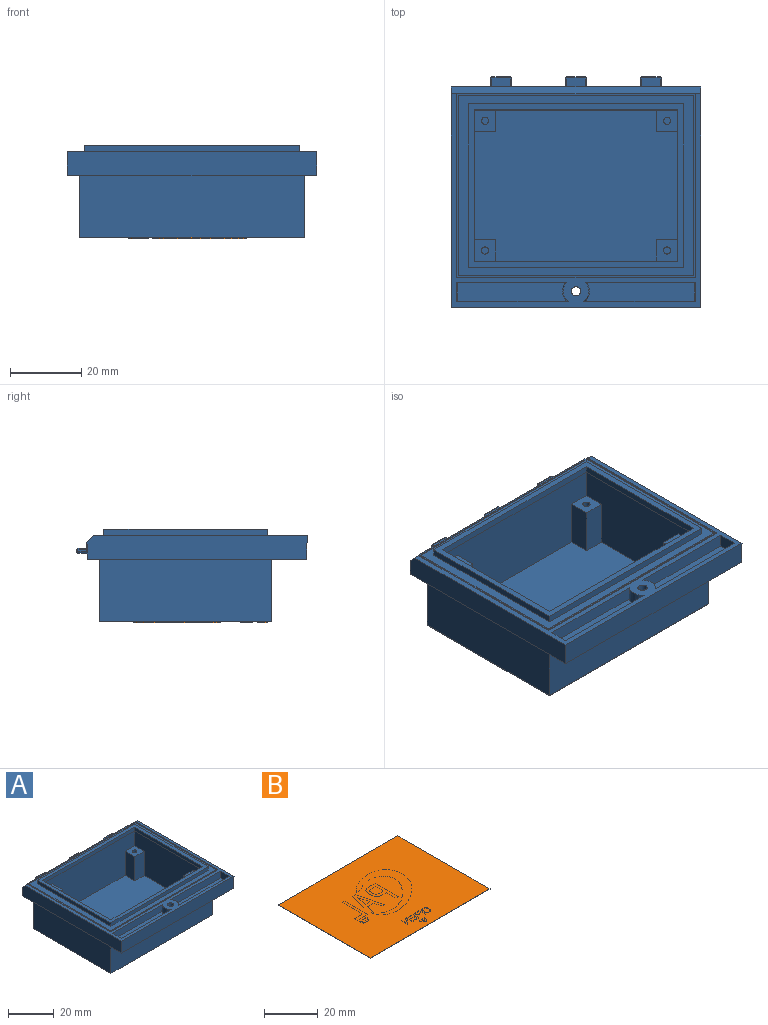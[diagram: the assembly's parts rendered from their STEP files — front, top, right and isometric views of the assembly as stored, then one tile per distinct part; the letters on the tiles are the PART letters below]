
ASSEMBLY  parts=2 mates=1
PART A: 126 faces, bbox 70x64.6x25.9 mm
  f0: plane 69.77x61.57mm, normal (0,0,-1), area 1213.8mm2, adj f1,f32,f48,f61,f83,f101,f102,f103
  f1: plane 69.94x4.55mm, normal (0,1,-0.02), area 187.9mm2, adj f0,f2,f8,f11,f20,f25,f27,f29
  f2: cylinder r=0.3mm len=2.58mm, axis (0,-1,0), area 1.2mm2, adj f1,f69,f77,f93
  f3: sphere r=0.3mm, area 0.1mm2, adj f30,f68,f82
  f4: sphere r=0.3mm, area 0.1mm2, adj f22,f23,f62
  f5: plane 5.2x2.47mm, normal (0,0,1), area 12.8mm2, adj f9,f24,f31,f81
  f6: cylinder r=0.3mm len=0.7mm, axis (0,0,1), area 0.3mm2, adj f20,f36,f66,f80
  f7: cylinder r=1.3mm len=5.2mm, axis (0,0,1), area 42.5mm2, adj f32,f85
  f8: cylinder r=0.3mm len=2.58mm, axis (0,-1,0), area 1.2mm2, adj f1,f29,f76,f93
  f9: plane 54x2.15mm, normal (0,1,0.01), area 104.9mm2, adj f5,f10,f11,f20,f23,f24,f25,f27
  f10: cylinder r=0.3mm len=2.47mm, axis (0,-1,0), area 1.2mm2, adj f9,f35,f70,f75
  f11: plane 15.2x0.11mm, normal (0,0,-1), area 1.7mm2, adj f1,f9,f20,f77
  f12: plane 66x0.2mm, normal (0,-1,0), area 13.2mm2, adj f37,f41,f44,f57
  f13: plane 42.4x1.9mm, normal (-1,0,0.02), area 80.5mm2, adj f16,f21,f52,f98
  f14: plane 45.8x1.9mm, normal (-1,0,0), area 87mm2, adj f17,f44,f52,f53
  f15: cylinder r=0.3mm len=0.7mm, axis (0,0,1), area 0.3mm2, adj f35,f72,f74,f75
  f16: plane 57.1x1.9mm, normal (0,-1,0.02), area 108.4mm2, adj f13,f52,f86,f97
  f17: plane 60.5x1.9mm, normal (0,-1,0), area 114.9mm2, adj f14,f44,f52,f54
  f18: sphere r=0.3mm, area 0.1mm2, adj f31,f81,f82
  f19: cylinder r=0.3mm len=0.7mm, axis (0,0,-1), area 0.3mm2, adj f60,f69,f73,f77
  f20: plane 2.58x0.7mm, normal (1,0,0), area 1.8mm2, adj f1,f6,f9,f11,f24,f79
  f21: plane 57.1x1.9mm, normal (0,1,0.02), area 108.4mm2, adj f13,f52,f86,f100
  f22: cylinder r=0.3mm len=0.7mm, axis (0,0,-1), area 0.3mm2, adj f4,f29,f73,f76
  f23: cylinder r=0.3mm len=2.47mm, axis (0,1,0), area 1.2mm2, adj f4,f9,f29,f71
  f24: cylinder r=0.3mm len=2.47mm, axis (0,-1,0), area 1.2mm2, adj f5,f9,f20,f80
  f25: plane 2.58x0.7mm, normal (-1,0,0), area 1.8mm2, adj f1,f9,f30,f31,f82,f89
  f26: plane 66.8x0.2mm, normal (0,-1,0), area 13.4mm2, adj f28,f34,f37,f85
  f27: plane 2.2x0.11mm, normal (-1,0,0), area 0.2mm2, adj f1,f9,f84,f87
  f28: plane 51.5x0.3mm, normal (-1,0,0), area 10.3mm2, adj f26,f37,f59,f84,f85
  f29: plane 2.58x0.7mm, normal (1,0,0), area 1.8mm2, adj f1,f8,f9,f22,f23,f88
  f30: cylinder r=0.3mm len=2.58mm, axis (0,-1,0), area 1.2mm2, adj f1,f3,f25,f94
  f31: cylinder r=0.3mm len=2.47mm, axis (0,1,0), area 1.2mm2, adj f5,f9,f18,f25
  f32: cone r=2.15mm half-angle=52.6deg, axis (0,0,-1), area 28.9mm2, adj f0,f7
  f33: plane 5.5x3.6mm, normal (-1,0,0.03), area 19.4mm2, adj f42,f45,f50,f85
  f34: plane 51.5x0.3mm, normal (1,0,0), area 10.3mm2, adj f26,f37,f59,f84,f85
  f35: plane 2.58x0.7mm, normal (1,0,0), area 1.8mm2, adj f1,f9,f10,f15,f89,f95
  f36: sphere r=0.3mm, area 0.1mm2, adj f6,f68,f79
  f37: plane 66.8x51.5mm, normal (0,0,1), area 94mm2, adj f12,f26,f28,f34,f41,f56,f57,f59
  f38: sphere r=0.3mm, area 0.1mm2, adj f39,f40,f64
  f39: cylinder r=0.3mm len=5.2mm, axis (1,0,0), area 2.5mm2, adj f38,f70,f72,f75
  f40: cylinder r=0.3mm len=2.47mm, axis (0,-1,0), area 1.2mm2, adj f9,f38,f70,f90
  f41: plane 50.7x0.2mm, normal (1,0,0), area 10.1mm2, adj f12,f37,f44,f56
  f42: plane 30.92x3.63mm, normal (0,-1,0.03), area 110.5mm2, adj f33,f50,f58,f85
  f43: plane 30.92x3.63mm, normal (0,-1,0.03), area 110.5mm2, adj f46,f49,f51,f85
  f44: plane 66x50.7mm, normal (0,0,1), area 575.3mm2, adj f12,f14,f17,f41,f53,f54,f56,f57
  f45: plane 31.39x3.64mm, normal (0,1,0.03), area 112mm2, adj f33,f50,f58,f85
  f46: plane 5.5x3.6mm, normal (1,0,0.03), area 19.4mm2, adj f43,f47,f49,f85
  f47: plane 31.39x3.64mm, normal (0,1,0.03), area 112mm2, adj f46,f49,f51,f85
  f48: plane 61.77x6.5mm, normal (1,0,-0.02), area 399.1mm2, adj f0,f1,f83,f84,f85
  f49: plane 30.87x5.25mm, normal (0,0,1), area 157.1mm2, adj f43,f46,f47,f51
  f50: plane 30.87x5.25mm, normal (0,0,1), area 157.1mm2, adj f33,f42,f45,f58
  f51: cone r=3.71mm half-angle=2deg, axis (0,0,-1), area 21.8mm2, adj f43,f47,f49,f85
  f52: plane 60.5x45.8mm, normal (0,0,1), area 349.9mm2, adj f13,f14,f16,f17,f21,f53,f54,f86
  f53: plane 60.5x1.9mm, normal (0,1,0), area 114.9mm2, adj f14,f44,f52,f54
  f54: plane 45.8x1.9mm, normal (1,0,0), area 87mm2, adj f17,f44,f52,f53
  f55: plane 2.2x0.11mm, normal (1,0,0), area 0.2mm2, adj f1,f9,f84,f88
  f56: plane 66x0.2mm, normal (0,1,0), area 13.2mm2, adj f37,f41,f44,f57
  f57: plane 50.7x0.2mm, normal (-1,0,0), area 10.1mm2, adj f12,f37,f44,f56
  f58: cone r=3.71mm half-angle=2deg, axis (0,0,-1), area 21.8mm2, adj f42,f45,f50,f85
  f59: plane 66.8x0.3mm, normal (0,1,0), area 20mm2, adj f28,f34,f37,f84
  f60: sphere r=0.3mm, area 0.1mm2, adj f19,f62,f78
  f61: plane 61.77x6.5mm, normal (-1,0,-0.02), area 399.1mm2, adj f0,f1,f83,f84,f85
  f62: cylinder r=0.3mm len=5.2mm, axis (1,0,0), area 2.5mm2, adj f4,f60,f71,f73
  f63: sphere r=0.3mm, area 0.1mm2, adj f64,f65,f91
  f64: cylinder r=0.3mm len=0.7mm, axis (0,0,1), area 0.3mm2, adj f38,f63,f72,f90
  f65: cylinder r=0.3mm len=5.2mm, axis (1,0,0), area 2.5mm2, adj f63,f72,f74,f92
  f66: plane 5.2x0.7mm, normal (0,1,0), area 3.6mm2, adj f6,f68,f81,f82
  f67: cylinder r=0.3mm len=5.2mm, axis (1,0,0), area 2.5mm2, adj f69,f73,f76,f93
  f68: cylinder r=0.3mm len=5.2mm, axis (1,0,0), area 2.5mm2, adj f3,f36,f66,f94
  f69: sphere r=0.3mm, area 0.1mm2, adj f2,f19,f67
  f70: plane 5.2x2.47mm, normal (0,0,1), area 12.8mm2, adj f9,f10,f39,f40
  f71: plane 5.2x2.47mm, normal (0,0,1), area 12.8mm2, adj f9,f23,f62,f78
  f72: plane 5.2x0.7mm, normal (0,1,0), area 3.6mm2, adj f15,f39,f64,f65
  f73: plane 5.2x0.7mm, normal (0,1,0), area 3.6mm2, adj f19,f22,f62,f67
  f74: sphere r=0.3mm, area 0.1mm2, adj f15,f65,f95
  f75: sphere r=0.3mm, area 0.1mm2, adj f10,f15,f39
  f76: sphere r=0.3mm, area 0.1mm2, adj f8,f22,f67
  f77: plane 2.58x0.7mm, normal (-1,0,0), area 1.8mm2, adj f1,f2,f9,f11,f19,f78
  f78: cylinder r=0.3mm len=2.47mm, axis (0,1,0), area 1.2mm2, adj f9,f60,f71,f77
  f79: cylinder r=0.3mm len=2.58mm, axis (0,1,0), area 1.2mm2, adj f1,f20,f36,f94
  f80: sphere r=0.3mm, area 0.1mm2, adj f6,f24,f81
  f81: cylinder r=0.3mm len=5.2mm, axis (1,0,0), area 2.5mm2, adj f5,f18,f66,f80
  f82: cylinder r=0.3mm len=0.7mm, axis (0,0,-1), area 0.3mm2, adj f3,f18,f25,f66
  f83: plane 70x6.5mm, normal (0,-1,-0.02), area 454.3mm2, adj f0,f48,f61,f85
  f84: plane 70x2.02mm, normal (0,0.7,0.71), area 188.2mm2, adj f1,f9,f27,f28,f34,f48,f55,f59
  f85: plane 70x59.8mm, normal (0,0,1), area 414.5mm2, adj f7,f26,f28,f33,f34,f42,f43,f45
  f86: plane 42.4x1.9mm, normal (1,0,0.02), area 80.5mm2, adj f16,f21,f52,f99
  f87: plane 3.1x0.11mm, normal (0,0,-1), area 0.3mm2, adj f1,f9,f27,f90
  f88: plane 3.1x0.11mm, normal (0,0,-1), area 0.3mm2, adj f1,f9,f29,f55
  f89: plane 15.2x0.11mm, normal (0,0,-1), area 1.7mm2, adj f1,f9,f25,f35
  f90: plane 2.58x0.7mm, normal (-1,0,0), area 1.8mm2, adj f1,f9,f40,f64,f87,f91
  f91: cylinder r=0.3mm len=2.58mm, axis (0,1,0), area 1.2mm2, adj f1,f63,f90,f92
  f92: plane 5.2x2.58mm, normal (0,0,-1), area 13.4mm2, adj f1,f65,f91,f95
  f93: plane 5.2x2.58mm, normal (0,0,-1), area 13.4mm2, adj f1,f2,f8,f67
  f94: plane 5.2x2.58mm, normal (0,0,-1), area 13.4mm2, adj f1,f30,f68,f79
  f95: cylinder r=0.3mm len=2.58mm, axis (0,1,0), area 1.2mm2, adj f1,f35,f74,f92
  f96: plane 57.03x42.33mm, normal (0,0,1), area 2272.4mm2, adj f97,f98,f99,f100,f106,f108,f111,f112
  f97: plane 57.03x21mm, normal (0,-1,0), area 1012.6mm2, adj f16,f96,f98,f99,f108,f109,f117,f119
  f98: plane 42.33x21mm, normal (-1,0,0), area 704.2mm2, adj f13,f96,f97,f100,f106,f109,f121,f124
  f99: plane 42.33x21mm, normal (1,0,0), area 703.9mm2, adj f86,f96,f97,f100,f111,f114,f116,f119
  f100: plane 57.03x21mm, normal (0,1,0), area 1013.8mm2, adj f21,f96,f98,f99,f112,f114,f122,f124
  f101: plane 63.1x17.5mm, normal (0,-1,0), area 1104.3mm2, adj f0,f102,f104,f105
  f102: plane 48.4x17.5mm, normal (-1,0,0), area 847mm2, adj f0,f101,f103,f105
  f103: plane 63.1x17.5mm, normal (0,1,0), area 1104.3mm2, adj f0,f102,f104,f105
  f104: plane 48.4x17.5mm, normal (1,0,0), area 847mm2, adj f0,f101,f103,f105
  f105: plane 63.1x48.4mm, normal (0,0,-1), area 3054mm2, adj f101,f102,f103,f104
  f106: plane 13x5.93mm, normal (0,-1,0), area 77.1mm2, adj f96,f98,f108,f109
  f107: cylinder r=1mm len=13mm, axis (0,0,-1), area 81.7mm2, adj f109,f110
  f108: plane 13x6mm, normal (-1,0,0), area 78mm2, adj f96,f97,f106,f109
  f109: plane 6x5.93mm, normal (0,0,1), area 32.5mm2, adj f97,f98,f106,f107,f108
  f110: plane 2x2mm, normal (0,0,1), area 3.1mm2, adj f107
  f111: plane 13x5.93mm, normal (0,1,0), area 77.1mm2, adj f96,f99,f112,f114
  f112: plane 13x5.93mm, normal (1,0,0), area 77.1mm2, adj f96,f100,f111,f114
  f113: cylinder r=1mm len=13mm, axis (0,0,-1), area 81.7mm2, adj f114,f115
  f114: plane 5.93x5.93mm, normal (0,0,1), area 32.1mm2, adj f99,f100,f111,f112,f113
  f115: plane 2x2mm, normal (0,0,1), area 3.1mm2, adj f113
  f116: plane 18x6mm, normal (0,-1,0), area 108mm2, adj f96,f99,f117,f119
  f117: plane 18x6mm, normal (1,0,0), area 108mm2, adj f96,f97,f116,f119
  f118: cylinder r=1mm len=18mm, axis (0,0,-1), area 113.1mm2, adj f119,f120
  f119: plane 6x6mm, normal (0,0,1), area 32.9mm2, adj f97,f99,f116,f117,f118
  f120: plane 2x2mm, normal (0,0,1), area 3.1mm2, adj f118
  f121: plane 18x5.93mm, normal (0,1,0), area 106.8mm2, adj f96,f98,f122,f124
  f122: plane 18x5.93mm, normal (-1,0,0), area 106.8mm2, adj f96,f100,f121,f124
  f123: cylinder r=1mm len=18mm, axis (0,0,-1), area 113.1mm2, adj f124,f125
  f124: plane 5.93x5.93mm, normal (0,0,1), area 32.1mm2, adj f98,f100,f121,f122,f123
  f125: plane 2x2mm, normal (0,0,1), area 3.1mm2, adj f123
PART B: 192 faces, bbox 63.1x48.4x0.4 mm
  f0: plane 2.86x0.41mm, normal (0,0,-1), area 1.1mm2, adj f8,f9,f10,f11
  f1: plane 0.56x0.41mm, normal (0,0,-1), area 0.1mm2, adj f12,f13,f14
  f2: plane 1.33x0.41mm, normal (0,0,-1), area 0.4mm2, adj f15,f16,f17,f18
  f3: plane 2.09x0.41mm, normal (0,0,-1), area 0.7mm2, adj f19,f20,f21,f22
  f4: plane 4.04x3.98mm, normal (0,0,-1), area 14.9mm2, adj f23,f24,f25,f26,f27,f28,f29
  f5: plane 5.29x2.59mm, normal (0,0,-1), area 6.9mm2, adj f30,f31,f32
  f6: plane 1.82x1.12mm, normal (0,0,-1), area 1.9mm2, adj f33,f34,f35,f36,f37,f38,f39,f40
  f7: plane 2.61x2.04mm, normal (0,0,-1), area 4.8mm2, adj f43,f44,f45,f46,f47,f48,f49,f50
  f8: plane 0.41x0.28mm, normal (-0.83,0.56,0), area 0.1mm2, adj f0,f9,f11,f63
  f9: plane 2.3x0.2mm, normal (0,1,0), area 0.5mm2, adj f0,f8,f10,f63
  f10: plane 0.41x0.28mm, normal (0.83,0.56,0), area 0.1mm2, adj f0,f9,f11,f63
  f11: plane 2.86x0.2mm, normal (0,-1,0), area 0.6mm2, adj f0,f8,f10,f63
  f12: plane 0.41x0.28mm, normal (0.83,0.56,0), area 0.1mm2, adj f1,f13,f14,f63
  f13: plane 0.56x0.2mm, normal (0,-1,0), area 0.1mm2, adj f1,f12,f14,f63
  f14: plane 0.41x0.28mm, normal (-0.83,0.56,0), area 0.1mm2, adj f1,f12,f13,f63
  f15: plane 0.41x0.28mm, normal (0.83,0.56,0), area 0.1mm2, adj f2,f16,f18,f63
  f16: plane 1.33x0.2mm, normal (0,-1,0), area 0.3mm2, adj f2,f15,f17,f63
  f17: plane 0.41x0.28mm, normal (-0.83,0.56,0), area 0.1mm2, adj f2,f16,f18,f63
  f18: plane 0.77x0.2mm, normal (0,1,0), area 0.2mm2, adj f2,f15,f17,f63
  f19: plane 0.41x0.28mm, normal (0.83,0.56,0), area 0.1mm2, adj f3,f20,f22,f63
  f20: plane 2.09x0.2mm, normal (0,-1,0), area 0.4mm2, adj f3,f19,f21,f63
  f21: plane 0.41x0.28mm, normal (-0.83,0.56,0), area 0.1mm2, adj f3,f20,f22,f63
  f22: plane 1.53x0.2mm, normal (0,1,0), area 0.3mm2, adj f3,f19,f21,f63
  f23: cylinder r=3.28mm len=0.99mm, axis (0,0,-1), area 0.3mm2, adj f4,f24,f29,f65
  f24: extruded ~1.99x1.68mm, area 0.9mm2, adj f4,f23,f25,f65
  f25: plane 2.3x0.3mm, normal (0,-1,0), area 0.7mm2, adj f4,f24,f26,f65
  f26: plane 4.04x0.3mm, normal (-1,0,0), area 1.2mm2, adj f4,f25,f27,f65
  f27: plane 1.82x0.3mm, normal (0,1,0), area 0.5mm2, adj f4,f26,f28,f65
  f28: extruded ~1.51x0.3mm, area 0.5mm2, adj f4,f27,f29,f65
  f29: cylinder r=1.62mm len=0.76mm, axis (0,0,-1), area 0.3mm2, adj f4,f23,f28,f65
  f30: plane 5.29x1.3mm, normal (-0.97,-0.24,0), area 1.6mm2, adj f5,f31,f32,f66
  f31: plane 2.59x0.3mm, normal (0,1,0), area 0.8mm2, adj f5,f30,f32,f66
  f32: plane 5.29x1.29mm, normal (0.97,-0.24,0), area 1.6mm2, adj f5,f30,f31,f66
  f33: plane 1.39x0.3mm, normal (0,1,0), area 0.4mm2, adj f6,f34,f42,f72
  f34: plane 0.3x0.22mm, normal (0.32,0.95,0), area 0.1mm2, adj f6,f33,f35,f72
  f35: plane 0.3x0.15mm, normal (0.71,0.7,0), area 0.1mm2, adj f6,f34,f36,f72
  f36: plane 0.3x0.22mm, normal (0.95,0.31,0), area 0.1mm2, adj f6,f35,f37,f72
  f37: plane 0.3x0.22mm, normal (1,0,0), area 0.1mm2, adj f6,f36,f38,f72
  f38: plane 0.3x0.22mm, normal (0.95,-0.31,0), area 0.1mm2, adj f6,f37,f39,f72
  f39: plane 0.3x0.15mm, normal (0.71,-0.7,0), area 0.1mm2, adj f6,f38,f40,f72
  f40: plane 0.3x0.22mm, normal (0.32,-0.95,0), area 0.1mm2, adj f6,f39,f41,f72
  f41: plane 1.39x0.3mm, normal (0,-1,0), area 0.4mm2, adj f6,f40,f42,f72
  f42: plane 1.12x0.3mm, normal (-1,0,0), area 0.3mm2, adj f6,f33,f41,f72
  f43: plane 0.58x0.3mm, normal (0,1,0), area 0.2mm2, adj f7,f44,f62,f73
  f44: plane 0.3x0.29mm, normal (0.25,0.97,0), area 0.1mm2, adj f7,f43,f45,f73
  f45: plane 0.3x0.22mm, normal (0.56,0.83,0), area 0.1mm2, adj f7,f44,f46,f73
  f46: plane 0.3x0.22mm, normal (0.84,0.55,0), area 0.1mm2, adj f7,f45,f47,f73
  f47: plane 0.3x0.3mm, normal (0.97,0.24,0), area 0.1mm2, adj f7,f46,f48,f73
  f48: plane 1.12x0.3mm, normal (1,0,0), area 0.3mm2, adj f7,f47,f49,f73
  f49: plane 0.3x0.3mm, normal (0.97,-0.24,0), area 0.1mm2, adj f7,f48,f50,f73
  f50: plane 0.3x0.22mm, normal (0.84,-0.55,0), area 0.1mm2, adj f7,f49,f51,f73
  f51: plane 0.3x0.22mm, normal (0.56,-0.83,0), area 0.1mm2, adj f7,f50,f52,f73
  f52: plane 0.3x0.29mm, normal (0.25,-0.97,0), area 0.1mm2, adj f7,f51,f53,f73
  f53: plane 0.58x0.3mm, normal (0,-1,0), area 0.2mm2, adj f7,f52,f54,f73
  f54: plane 0.3x0.29mm, normal (-0.25,-0.97,0), area 0.1mm2, adj f7,f53,f55,f73
  f55: plane 0.3x0.22mm, normal (-0.56,-0.83,0), area 0.1mm2, adj f7,f54,f56,f73
  f56: plane 0.3x0.22mm, normal (-0.84,-0.55,0), area 0.1mm2, adj f7,f55,f57,f73
  f57: plane 0.3x0.3mm, normal (-0.97,-0.24,0), area 0.1mm2, adj f7,f56,f58,f73
  f58: plane 1.12x0.3mm, normal (-1,0,0), area 0.3mm2, adj f7,f57,f59,f73
  f59: plane 0.3x0.3mm, normal (-0.97,0.24,0), area 0.1mm2, adj f7,f58,f60,f73
  f60: plane 0.3x0.22mm, normal (-0.84,0.55,0), area 0.1mm2, adj f7,f59,f61,f73
  f61: plane 0.3x0.22mm, normal (-0.56,0.83,0), area 0.1mm2, adj f7,f60,f62,f73
  f62: plane 0.3x0.29mm, normal (-0.25,0.97,0), area 0.1mm2, adj f7,f43,f61,f73
  f63: plane 3.8x2.8mm, normal (0,0,-1), area 3mm2, adj f8,f9,f10,f11,f12,f13,f14,f15
  f64: plane 26.09x24.59mm, normal (0,0,-1), area 159.6mm2, adj f77,f78,f79,f80
  f65: plane 12.21x6.45mm, normal (0,0,-1), area 33.8mm2, adj f23,f24,f25,f26,f27,f28,f29,f81
  f66: plane 12.2x7.77mm, normal (0,0,-1), area 34.6mm2, adj f30,f31,f32,f91,f92,f93,f94,f95
  f67: plane 12.2x5.55mm, normal (0,0,-1), area 21.7mm2, adj f99,f100,f101,f102,f103,f104
  f68: plane 2x1.58mm, normal (0,0,-1), area 0.8mm2, adj f105,f106,f107,f108,f109,f110,f111,f112
  f69: plane 2x2mm, normal (0,0,-1), area 2mm2, adj f113,f114,f115,f116,f117,f118,f119,f120
  f70: plane 3.5x2.92mm, normal (0,0,-1), area 4.7mm2, adj f126,f127,f128,f129,f130,f131,f132,f133
  f71: plane 3.5x2.63mm, normal (0,0,-1), area 4.3mm2, adj f136,f137,f138,f139,f140,f141,f142,f143
  f72: plane 3.5x2.7mm, normal (0,0,-1), area 3.5mm2, adj f33,f34,f35,f36,f37,f38,f39,f40
  f73: plane 3.5x2.92mm, normal (0,0,-1), area 4.1mm2, adj f43,f44,f45,f46,f47,f48,f49,f50
  f74: plane 2.8x1.9mm, normal (-0.83,-0.56,0), area 1mm2, adj f63,f75,f76,f186
  f75: plane 3.8x0.3mm, normal (0,1,0), area 1.1mm2, adj f63,f74,f76,f186
  f76: plane 2.8x1.9mm, normal (0.83,-0.56,0), area 1mm2, adj f63,f74,f75,f186
  f77: plane 2.16x0.3mm, normal (0,-1,0), area 0.6mm2, adj f64,f78,f80,f186
  f78: extruded ~25.91x24.22mm, area 19.1mm2, adj f64,f77,f79,f186
  f79: plane 0.48x0.3mm, normal (0,1,0), area 0.1mm2, adj f64,f78,f80,f186
  f80: extruded ~21.1x19.29mm, area 14.1mm2, adj f64,f77,f79,f186
  f81: extruded ~1.24x0.89mm, area 0.5mm2, adj f65,f82,f90,f186
  f82: extruded ~1.99x0.48mm, area 0.6mm2, adj f65,f81,f83,f186
  f83: plane 3.26x0.3mm, normal (0,1,0), area 1mm2, adj f65,f82,f84,f186
  f84: plane 12.2x0.3mm, normal (1,0,0), area 3.7mm2, adj f65,f83,f85,f186
  f85: plane 1.23x0.3mm, normal (0,-1,0), area 0.4mm2, adj f65,f84,f86,f186
  f86: plane 5.04x0.3mm, normal (-1,0,0), area 1.5mm2, adj f65,f85,f87,f186
  f87: plane 2.46x0.3mm, normal (0,-1,0), area 0.7mm2, adj f65,f86,f88,f186
  f88: extruded ~2.05x0.98mm, area 0.7mm2, adj f65,f87,f89,f186
  f89: extruded ~2.66x0.7mm, area 0.8mm2, adj f65,f88,f90,f186
  f90: extruded ~1.8x0.3mm, area 0.5mm2, adj f65,f81,f89,f186
  f91: plane 1.37x0.3mm, normal (0,-1,0), area 0.4mm2, adj f66,f92,f98,f186
  f92: plane 3.53x0.85mm, normal (-0.97,-0.23,0), area 1.1mm2, adj f66,f91,f93,f186
  f93: plane 3.32x0.3mm, normal (0,-1,0), area 1mm2, adj f66,f92,f94,f186
  f94: plane 3.53x0.85mm, normal (0.97,-0.23,0), area 1.1mm2, adj f66,f93,f95,f186
  f95: plane 1.37x0.3mm, normal (0,-1,0), area 0.4mm2, adj f66,f94,f96,f186
  f96: plane 12.2x3.16mm, normal (-0.97,0.25,0), area 3.8mm2, adj f66,f95,f97,f186
  f97: plane 1.44x0.3mm, normal (0,1,0), area 0.4mm2, adj f66,f96,f98,f186
  f98: plane 12.2x3.16mm, normal (0.97,0.25,0), area 3.8mm2, adj f66,f91,f97,f186
  f99: plane 5.55x0.3mm, normal (0,-1,0), area 1.7mm2, adj f67,f100,f104,f186
  f100: plane 1.56x0.3mm, normal (-1,0,0), area 0.5mm2, adj f67,f99,f101,f186
  f101: plane 4.32x0.3mm, normal (0,1,0), area 1.3mm2, adj f67,f100,f102,f186
  f102: plane 10.64x0.3mm, normal (-1,0,0), area 3.2mm2, adj f67,f101,f103,f186
  f103: plane 1.23x0.3mm, normal (0,1,0), area 0.4mm2, adj f67,f102,f104,f186
  f104: plane 12.2x0.3mm, normal (1,0,0), area 3.7mm2, adj f67,f99,f103,f186
  f105: plane 0.67x0.3mm, normal (0,-1,0), area 0.2mm2, adj f68,f106,f112,f186
  f106: plane 0.3x0.21mm, normal (-1,0,0), area 0.1mm2, adj f68,f105,f107,f186
  f107: plane 1.58x0.3mm, normal (0,1,0), area 0.5mm2, adj f68,f106,f108,f186
  f108: plane 0.3x0.21mm, normal (1,0,0), area 0.1mm2, adj f68,f107,f109,f186
  f109: plane 0.67x0.3mm, normal (0,-1,0), area 0.2mm2, adj f68,f108,f110,f186
  f110: plane 1.79x0.3mm, normal (1,0,0), area 0.5mm2, adj f68,f109,f111,f186
  f111: plane 0.3x0.25mm, normal (0,-1,0), area 0.1mm2, adj f68,f110,f112,f186
  f112: plane 1.79x0.3mm, normal (-1,0,0), area 0.5mm2, adj f68,f105,f111,f186
  f113: plane 1.57x0.3mm, normal (-1,0,0), area 0.5mm2, adj f69,f114,f125,f186
  f114: plane 1.57x0.58mm, normal (0.94,-0.35,0), area 0.5mm2, adj f69,f113,f115,f186
  f115: plane 0.33x0.3mm, normal (0,-1,0), area 0.1mm2, adj f69,f114,f116,f186
  f116: plane 1.57x0.58mm, normal (-0.94,-0.35,0), area 0.5mm2, adj f69,f115,f117,f186
  f117: plane 1.57x0.3mm, normal (1,0,0), area 0.5mm2, adj f69,f116,f118,f186
  f118: plane 0.3x0.25mm, normal (0,-1,0), area 0.1mm2, adj f69,f117,f119,f186
  f119: plane 2x0.3mm, normal (-1,0,0), area 0.6mm2, adj f69,f118,f120,f186
  f120: plane 0.38x0.3mm, normal (0,1,0), area 0.1mm2, adj f69,f119,f121,f186
  f121: plane 1.79x0.63mm, normal (0.94,0.33,0), area 0.6mm2, adj f69,f120,f122,f186
  f122: plane 1.79x0.63mm, normal (-0.94,0.33,0), area 0.6mm2, adj f69,f121,f123,f186
  f123: plane 0.38x0.3mm, normal (0,1,0), area 0.1mm2, adj f69,f122,f124,f186
  f124: plane 2x0.3mm, normal (1,0,0), area 0.6mm2, adj f69,f123,f125,f186
  f125: plane 0.3x0.25mm, normal (0,-1,0), area 0.1mm2, adj f69,f113,f124,f186
  f126: plane 3.05x1.82mm, normal (0.86,-0.51,0), area 1.1mm2, adj f70,f127,f135,f186
  f127: plane 0.66x0.3mm, normal (0,-1,0), area 0.2mm2, adj f70,f126,f128,f186
  f128: plane 3.5x0.3mm, normal (-1,0,0), area 1mm2, adj f70,f127,f129,f186
  f129: plane 0.44x0.3mm, normal (0,1,0), area 0.1mm2, adj f70,f128,f130,f186
  f130: plane 2.98x0.3mm, normal (1,0,0), area 0.9mm2, adj f70,f129,f131,f186
  f131: plane 2.98x1.82mm, normal (-0.85,0.52,0), area 1mm2, adj f70,f130,f132,f186
  f132: plane 0.66x0.3mm, normal (0,1,0), area 0.2mm2, adj f70,f131,f133,f186
  f133: plane 3.5x0.3mm, normal (1,0,0), area 1mm2, adj f70,f132,f134,f186
  f134: plane 0.44x0.3mm, normal (0,-1,0), area 0.1mm2, adj f70,f133,f135,f186
  f135: plane 3.05x0.3mm, normal (-1,0,0), area 0.9mm2, adj f70,f126,f134,f186
  f136: plane 2.63x0.3mm, normal (0,-1,0), area 0.8mm2, adj f71,f137,f147,f186
  f137: plane 0.45x0.3mm, normal (-1,0,0), area 0.1mm2, adj f71,f136,f138,f186
  f138: plane 2.19x0.3mm, normal (0,1,0), area 0.7mm2, adj f71,f137,f139,f186
  f139: plane 1.19x0.3mm, normal (-1,0,0), area 0.4mm2, adj f71,f138,f140,f186
  f140: plane 1.9x0.3mm, normal (0,-1,0), area 0.6mm2, adj f71,f139,f141,f186
  f141: plane 0.45x0.3mm, normal (-1,0,0), area 0.1mm2, adj f71,f140,f142,f186
  f142: plane 1.9x0.3mm, normal (0,1,0), area 0.6mm2, adj f71,f141,f143,f186
  f143: plane 0.97x0.3mm, normal (-1,0,0), area 0.3mm2, adj f71,f142,f144,f186
  f144: plane 2.19x0.3mm, normal (0,-1,0), area 0.7mm2, adj f71,f143,f145,f186
  f145: plane 0.45x0.3mm, normal (-1,0,0), area 0.1mm2, adj f71,f144,f146,f186
  f146: plane 2.63x0.3mm, normal (0,1,0), area 0.8mm2, adj f71,f145,f147,f186
  f147: plane 3.5x0.3mm, normal (1,0,0), area 1mm2, adj f71,f136,f146,f186
  f148: plane 0.36x0.3mm, normal (-0.2,-0.98,0), area 0.1mm2, adj f72,f149,f161,f186
  f149: plane 0.3x0.29mm, normal (-0.61,-0.79,0), area 0.1mm2, adj f72,f148,f150,f186
  f150: plane 0.3x0.3mm, normal (-0.81,-0.59,0), area 0.1mm2, adj f72,f149,f151,f186
  f151: plane 0.3x0.22mm, normal (-0.95,-0.31,0), area 0.1mm2, adj f72,f150,f152,f186
  f152: plane 0.3x0.3mm, normal (-1,0,0), area 0.1mm2, adj f72,f151,f153,f186
  f153: plane 0.3x0.22mm, normal (-0.95,0.31,0), area 0.1mm2, adj f72,f152,f154,f186
  f154: plane 0.3x0.3mm, normal (-0.81,0.59,0), area 0.1mm2, adj f72,f153,f155,f186
  f155: plane 0.3x0.29mm, normal (-0.61,0.79,0), area 0.1mm2, adj f72,f154,f156,f186
  f156: plane 0.36x0.3mm, normal (-0.2,0.98,0), area 0.1mm2, adj f72,f155,f157,f186
  f157: plane 1.75x0.3mm, normal (0,1,0), area 0.5mm2, adj f72,f156,f158,f186
  f158: plane 3.5x0.3mm, normal (1,0,0), area 1mm2, adj f72,f157,f159,f186
  f159: plane 0.44x0.3mm, normal (0,-1,0), area 0.1mm2, adj f72,f158,f160,f186
  f160: plane 1.56x0.3mm, normal (-1,0,0), area 0.5mm2, adj f72,f159,f161,f186
  f161: plane 1.31x0.3mm, normal (0,-1,0), area 0.4mm2, adj f72,f148,f160,f186
  f162: plane 0.3x0.3mm, normal (-0.71,-0.7,0), area 0.1mm2, adj f73,f163,f185,f186
  f163: plane 0.3x0.3mm, normal (-0.9,-0.44,0), area 0.1mm2, adj f73,f162,f164,f186
  f164: plane 0.37x0.3mm, normal (-0.98,-0.19,0), area 0.1mm2, adj f73,f163,f165,f186
  f165: plane 1.12x0.3mm, normal (-1,0,0), area 0.3mm2, adj f73,f164,f166,f186
  f166: plane 0.37x0.3mm, normal (-0.98,0.19,0), area 0.1mm2, adj f73,f165,f167,f186
  f167: plane 0.3x0.3mm, normal (-0.9,0.44,0), area 0.1mm2, adj f73,f166,f168,f186
  f168: plane 0.3x0.3mm, normal (-0.71,0.7,0), area 0.1mm2, adj f73,f167,f169,f186
  f169: plane 0.3x0.29mm, normal (-0.45,0.89,0), area 0.1mm2, adj f73,f168,f170,f186
  f170: plane 0.36x0.3mm, normal (-0.2,0.98,0), area 0.1mm2, adj f73,f169,f171,f186
  f171: plane 0.58x0.3mm, normal (0,1,0), area 0.2mm2, adj f73,f170,f172,f186
  f172: plane 0.36x0.3mm, normal (0.2,0.98,0), area 0.1mm2, adj f73,f171,f173,f186
  f173: plane 0.3x0.29mm, normal (0.45,0.89,0), area 0.1mm2, adj f73,f172,f174,f186
  f174: plane 0.3x0.3mm, normal (0.71,0.7,0), area 0.1mm2, adj f73,f173,f175,f186
  f175: plane 0.3x0.3mm, normal (0.9,0.44,0), area 0.1mm2, adj f73,f174,f176,f186
  f176: plane 0.37x0.3mm, normal (0.98,0.19,0), area 0.1mm2, adj f73,f175,f177,f186
  f177: plane 1.12x0.3mm, normal (1,0,0), area 0.3mm2, adj f73,f176,f178,f186
  f178: plane 0.37x0.3mm, normal (0.98,-0.19,0), area 0.1mm2, adj f73,f177,f179,f186
  f179: plane 0.3x0.3mm, normal (0.9,-0.44,0), area 0.1mm2, adj f73,f178,f180,f186
  f180: plane 0.3x0.3mm, normal (0.71,-0.7,0), area 0.1mm2, adj f73,f179,f181,f186
  f181: plane 0.3x0.29mm, normal (0.45,-0.89,0), area 0.1mm2, adj f73,f180,f182,f186
  f182: plane 0.36x0.3mm, normal (0.2,-0.98,0), area 0.1mm2, adj f73,f181,f183,f186
  f183: plane 0.58x0.3mm, normal (0,-1,0), area 0.2mm2, adj f73,f182,f184,f186
  f184: plane 0.36x0.3mm, normal (-0.2,-0.98,0), area 0.1mm2, adj f73,f183,f185,f186
  f185: plane 0.3x0.29mm, normal (-0.45,-0.89,0), area 0.1mm2, adj f73,f162,f184,f186
  f186: plane 63.11x48.41mm, normal (0,0,-1), area 2751.1mm2, adj f74,f75,f76,f77,f78,f79,f80,f81
  f187: plane 63.1x0.1mm, normal (0,-1,0), area 6.3mm2, adj f186,f188,f189,f191
  f188: plane 48.4x0.1mm, normal (-1,0,0), area 4.8mm2, adj f186,f187,f190,f191
  f189: plane 48.4x0.1mm, normal (1,0,0), area 4.8mm2, adj f186,f187,f190,f191
  f190: plane 63.1x0.1mm, normal (0,1,0), area 6.3mm2, adj f186,f188,f189,f191
  f191: plane 63.1x48.4mm, normal (0,0,1), area 3054mm2, adj f187,f188,f189,f190
PLACE A t=(109.52,-14.4,-8.26)mm
PLACE B t=(109.52,-14.4,-25.86)mm
MATE planar A.f105 <-> B.f191  axis (0,0,-1) through (109.52,-11.2,-25.76)mm
